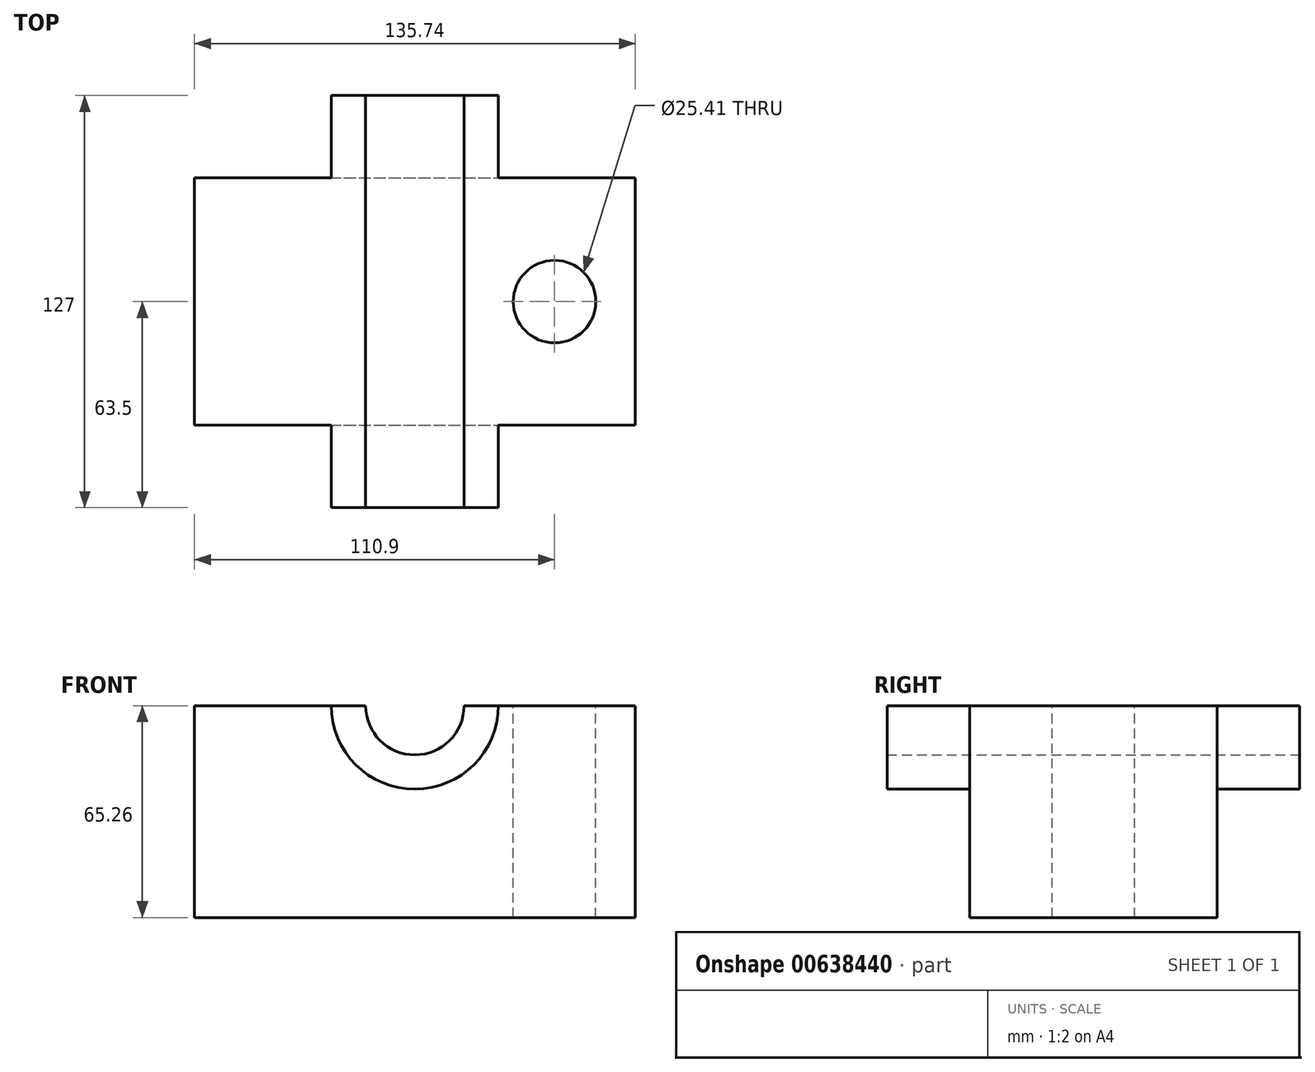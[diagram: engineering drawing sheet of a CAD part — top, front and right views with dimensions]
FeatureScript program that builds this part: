
annotation { "Feature Type Name" : "Feature", "Feature Type Description" : "" }
export const myFeature = defineFeature(function(context is Context, id is Id, definition is map)
    precondition{}
    {
        {
            var Q0;
            Q0=qCreatedBy(makeId("Front.planeOp"),FACE);
            var sketch = newSketch(context, id + "F0", { "sketchPlane" : qUnion([Q0])});
            skLineSegment(sketch, "E0.bottom", {"start": v(-67.87, 32.63) * mm, "end": v(-15.16, 32.63) * mm});
            skLineSegment(sketch, "E0.top", {"start": v(-67.87, -32.63) * mm, "end": v(67.87, -32.63) * mm});
            skLineSegment(sketch, "E0.left", {"start": v(-67.87, 32.63) * mm, "end": v(-67.87, -32.63) * mm});
            skLineSegment(sketch, "E0.right", {"start": v(67.87, 32.63) * mm, "end": v(67.87, -32.63) * mm});
            skPoint(sketch, "E0.middle", {"position": v(0, 0) * mm});
            skArc(sketch, "E1", {"start": v(-25.72, 32.63) * mm, "mid": v(0, 6.9) * mm, "end": v(25.72, 32.63) * mm});
            skArc(sketch, "E2", {"start": v(-15.16, 32.63) * mm, "mid": v(0, 17.47) * mm, "end": v(15.16, 32.63) * mm});
            skLineSegment(sketch, "E3.trimOffspring", {"start": v(15.16, 32.63) * mm, "end": v(67.87, 32.63) * mm});
            skSolve(sketch);
        }
        {
            var Q0;
            Q0=makeQuery(id+"F0.imprint","IMPRINT",FACE,{"disambiguationData":[TD([[makeQuery(id+"F0.imprint","IMPRINT",EDGE,{"derivedFrom":sQuery(id+"F0.wireOp",EDGE,"E0.top")}),1.0]])]});
            extrude(context, id + "F1", {"entities" : qUnion([Q0]), "endBound" : BoundingType.SYMMETRIC, "depth" : 76.2 * mm, "offsetDistance" : 25.4 * mm});
        }
        {
            var Q0;
            {var subQ2=sQuery(id+"F0.wireOp",EDGE,"E1");Q0=makeQuery(id+"F0.imprint","IMPRINT",FACE,{"disambiguationData":[TD([[makeQuery(id+"F0.imprint","IMPRINT",EDGE,{"derivedFrom":subQ2}),1.0]])]});}
            extrude(context, id + "F2", {"entities" : qUnion([Q0]), "operationType" : NewBodyOperationType.ADD, "endBound" : BoundingType.SYMMETRIC, "depth" : 127 * mm, "offsetDistance" : 25.4 * mm});
        }
        {
            var Q0;
            {var subQ0=sQuery(id+"F0.wireOp",EDGE,"E3.trimOffspring");Q0=makeQuery(id+"F2.boolean.opBoolean","MERGE",FACE,{"derivedFrom":[makeQuery(id+"F1.opExtrude","SWEPT_FACE",FACE,{"disambiguationData":[OSD([subQ0])]}),makeQuery(id+"F2.opExtrude","SWEPT_FACE",FACE,{"disambiguationData":[OSD([subQ0])]})]});}
            var sketch = newSketch(context, id + "F3", { "sketchPlane" : qUnion([Q0])});
            skCircle(sketch, "E4", {"center": v(43.03, 0) * mm, "radius": 12.7 * mm});
            skPoint(sketch, "E4.centerSnap0", {"position": v(67.87, 0) * mm});
            skCircle(sketch, "E5.MirrorC", {"center": v(-43.03, 0) * mm, "radius": 12.7 * mm});
            skSolve(sketch);
        }
        {
            var Q0;
            Q0=makeQuery(id+"F3.imprint","IMPRINT",FACE,{"disambiguationData":[TD([[makeQuery(id+"F3.imprint","IMPRINT",EDGE,{"derivedFrom":sQuery(id+"F3.wireOp",EDGE,"E5.MirrorC")}),-1.0]])]});
            var Q1;
            Q1=makeQuery(id+"F3.imprint","IMPRINT",FACE,{"disambiguationData":[TD([[makeQuery(id+"F3.imprint","IMPRINT",EDGE,{"derivedFrom":sQuery(id+"F3.wireOp",EDGE,"E4")}),1.0]])]});
            extrude(context, id + "F4", {"entities" : qUnion([Q0, Q1]), "operationType" : NewBodyOperationType.REMOVE, "endBound" : BoundingType.THROUGH_ALL, "oppositeDirection" : true, "depth" : 25.4 * mm, "offsetDistance" : 25.4 * mm});
        }
    });
